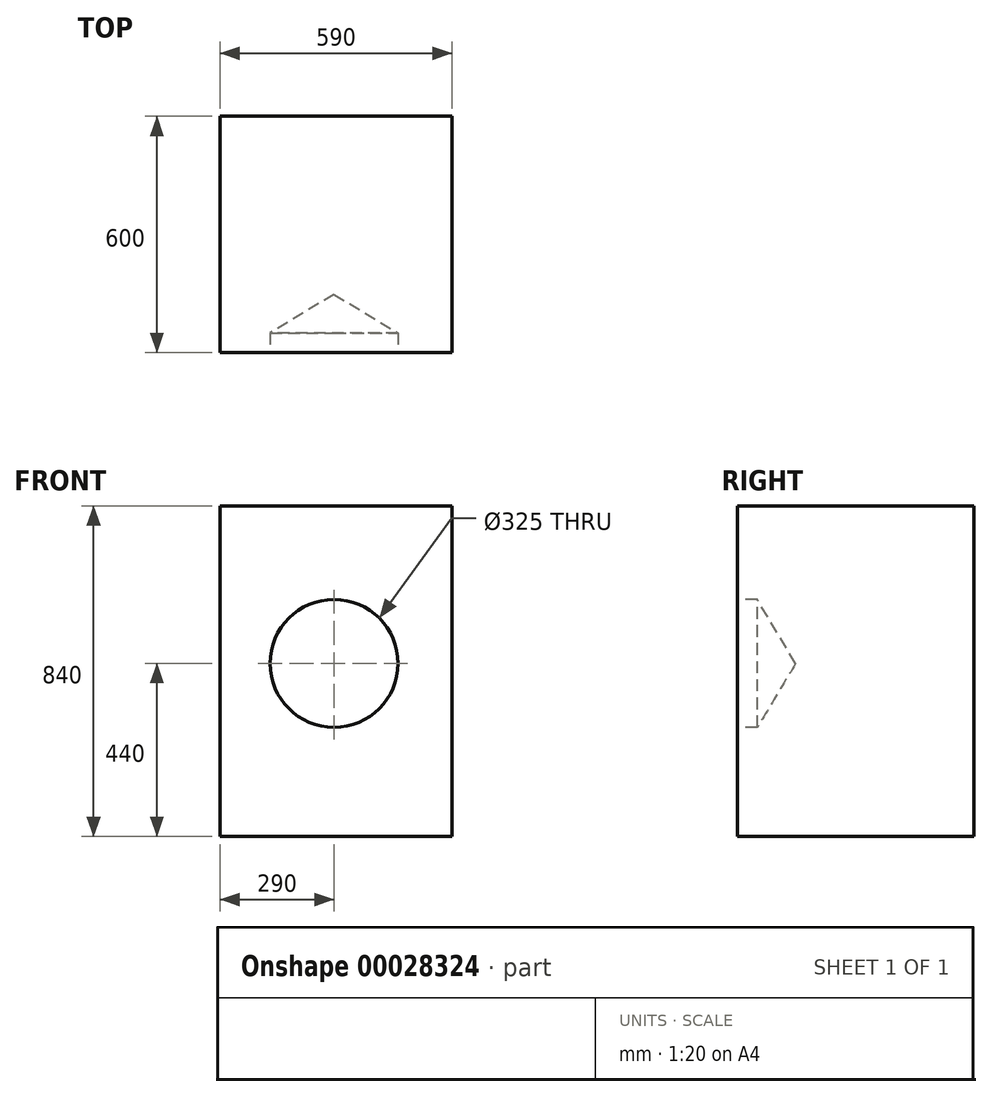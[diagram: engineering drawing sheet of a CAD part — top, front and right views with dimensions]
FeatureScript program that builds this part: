
annotation { "Feature Type Name" : "Feature", "Feature Type Description" : "" }
export const myFeature = defineFeature(function(context is Context, id is Id, definition is map)
    precondition{}
    {
        {
            var Q0;
            Q0=qCreatedBy(makeId("Top.planeOp"),FACE);
            var sketch = newSketch(context, id + "F0", { "sketchPlane" : qUnion([Q0])});
            skLineSegment(sketch, "E0.bottom", {"start": v(0, 0) * mm, "end": v(590, 0) * mm});
            skLineSegment(sketch, "E0.top", {"start": v(0, -600) * mm, "end": v(590, -600) * mm});
            skLineSegment(sketch, "E0.left", {"start": v(0, 0) * mm, "end": v(0, -600) * mm});
            skLineSegment(sketch, "E0.right", {"start": v(590, 0) * mm, "end": v(590, -600) * mm});
            skSolve(sketch);
        }
        {
            var Q0;
            Q0=makeQuery(id+"F0.imprint","IMPRINT",FACE,{"disambiguationData":[TD([[makeQuery(id+"F0.imprint","IMPRINT",EDGE,{"derivedFrom":sQuery(id+"F0.wireOp",EDGE,"E0.bottom")}),-1.0]])]});
            extrude(context, id + "F1", {"entities" : qUnion([Q0]), "depth" : 840 * mm});
        }
        {
            var Q0;
            Q0=makeQuery(id+"F1.opExtrude","SWEPT_FACE",FACE,{"disambiguationData":[OSD([sQuery(id+"F0.wireOp",EDGE,"E0.top")])]});
            var sketch = newSketch(context, id + "F2", { "sketchPlane" : qUnion([Q0])});
            skCircle(sketch, "E1", {"center": v(290, 440) * mm, "radius": 162.5 * mm});
            skSolve(sketch);
        }
        {
            var Q0;
            Q0=sQuery(id+"F2.wireOp",VERTEX,"E1.center");
            var Q1;
            Q1=makeQuery(id+"F1.opExtrude","SWEPT_BODY",BODY,{"disambiguationData":[OSD([sQuery(id+"F0.wireOp",EDGE,"E0.bottom"),sQuery(id+"F0.wireOp",EDGE,"E0.top"),sQuery(id+"F0.wireOp",EDGE,"E0.left"),sQuery(id+"F0.wireOp",EDGE,"E0.right")])]});
            hole(context, id + "F3", {"style" : HoleStyle.SIMPLE, "holeDiameter" : 325 * mm, "endStyle" : HoleEndStyle.BLIND, "holeDepth" : 50 * mm, "locations" : qUnion([Q0]), "scope" : qUnion([Q1])});
        }
    });
